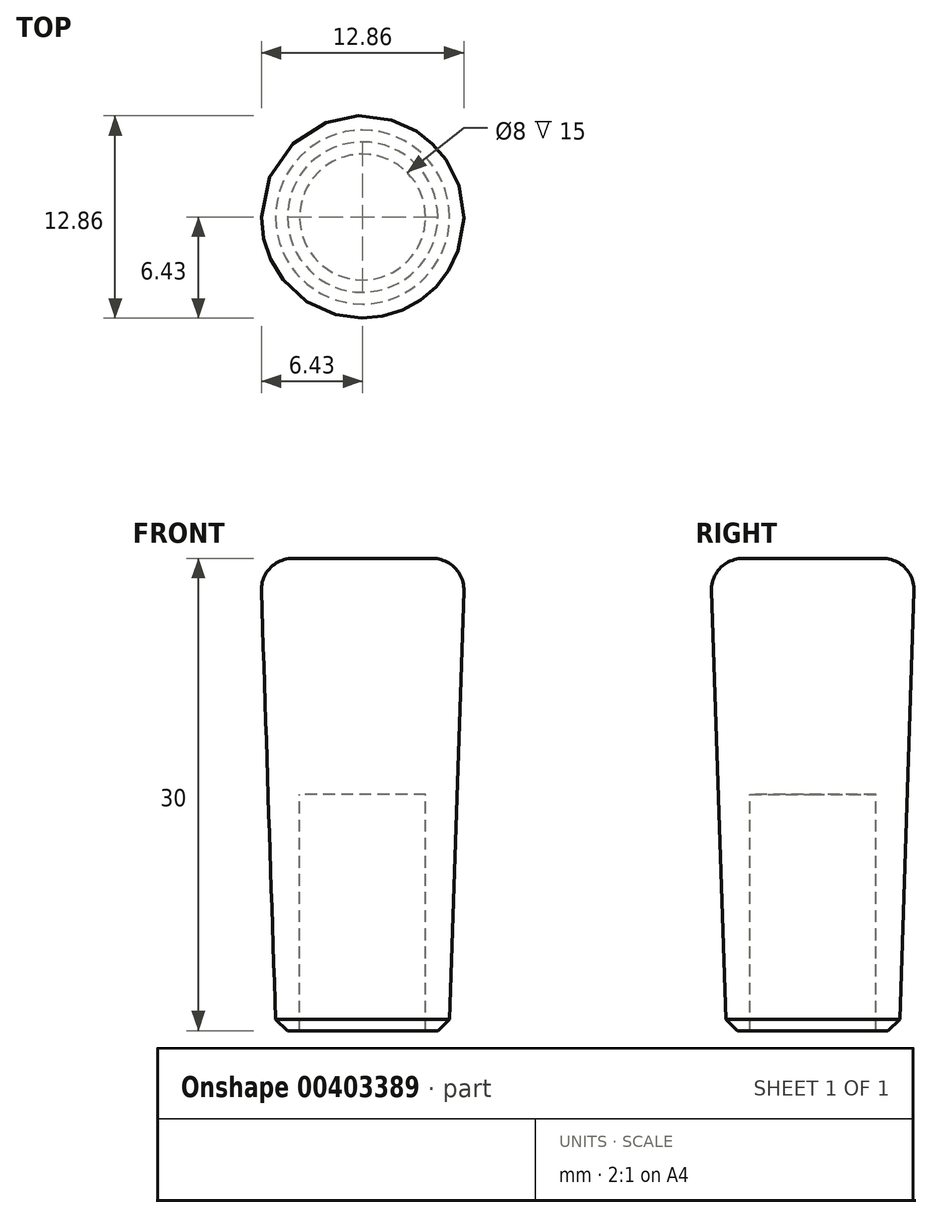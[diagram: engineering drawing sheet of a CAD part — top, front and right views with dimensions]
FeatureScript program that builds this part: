
annotation { "Feature Type Name" : "Feature", "Feature Type Description" : "" }
export const myFeature = defineFeature(function(context is Context, id is Id, definition is map)
    precondition{}
    {
        {
            var Q0;
            Q0=qCreatedBy(makeId("Front.planeOp"),FACE);
            var sketch = newSketch(context, id + "F0", { "sketchPlane" : qUnion([Q0])});
            skLineSegment(sketch, "E0", {"start": v(0, 23.35) * mm, "end": v(0, -23.23) * mm, "construction": true});
            skLineSegment(sketch, "E1", {"start": v(6.5, 30) * mm, "end": v(0, 30) * mm});
            skLineSegment(sketch, "E2", {"start": v(0, 30) * mm, "end": v(0, 15) * mm});
            skLineSegment(sketch, "E3", {"start": v(0, 15) * mm, "end": v(4, 15) * mm});
            skLineSegment(sketch, "E4", {"start": v(4, 15) * mm, "end": v(4, 0) * mm});
            skLineSegment(sketch, "E5", {"start": v(4, 0) * mm, "end": v(5.5, 0) * mm});
            skLineSegment(sketch, "E6", {"start": v(5.5, 0) * mm, "end": v(6.5, 30) * mm});
            skSolve(sketch);
        }
        {
            var Q0;
            Q0=makeQuery(id+"F0.imprint","IMPRINT",FACE,{"disambiguationData":[TD([[makeQuery(id+"F0.imprint","IMPRINT",EDGE,{"derivedFrom":sQuery(id+"F0.wireOp",EDGE,"E1")}),1.0]])]});
            var Q1;
            Q1=sQuery(id+"F0.wireOp",EDGE,"E0");
            revolve(context, id + "F1", {"entities" : qUnion([Q0]), "axis" : qUnion([Q1]), "revolveType" : RevolveType.FULL});
        }
        {
            var Q0;
            Q0=makeQuery(id+"F1.opRevolve","SWEPT_EDGE",EDGE,{"disambiguationData":[OSD([sQuery(id+"F0.wireOp",EDGE,"E1"),sQuery(id+"F0.wireOp",EDGE,"E6")])]});
            fillet(context, id + "F2", {"entities" : qUnion([Q0]), "radius" : 2 * mm, "tangentPropagation" : true, "allowEdgeOverflow" : false});
        }
        {
            var Q0;
            Q0=makeQuery(id+"F1.opRevolve","SWEPT_EDGE",EDGE,{"disambiguationData":[OSD([sQuery(id+"F0.wireOp",EDGE,"E5"),sQuery(id+"F0.wireOp",EDGE,"E6")])]});
            chamfer(context, id + "F3", {"entities" : qUnion([Q0]), "width" : 0.75 * mm, "tangentPropagation" : true});
        }
    });
